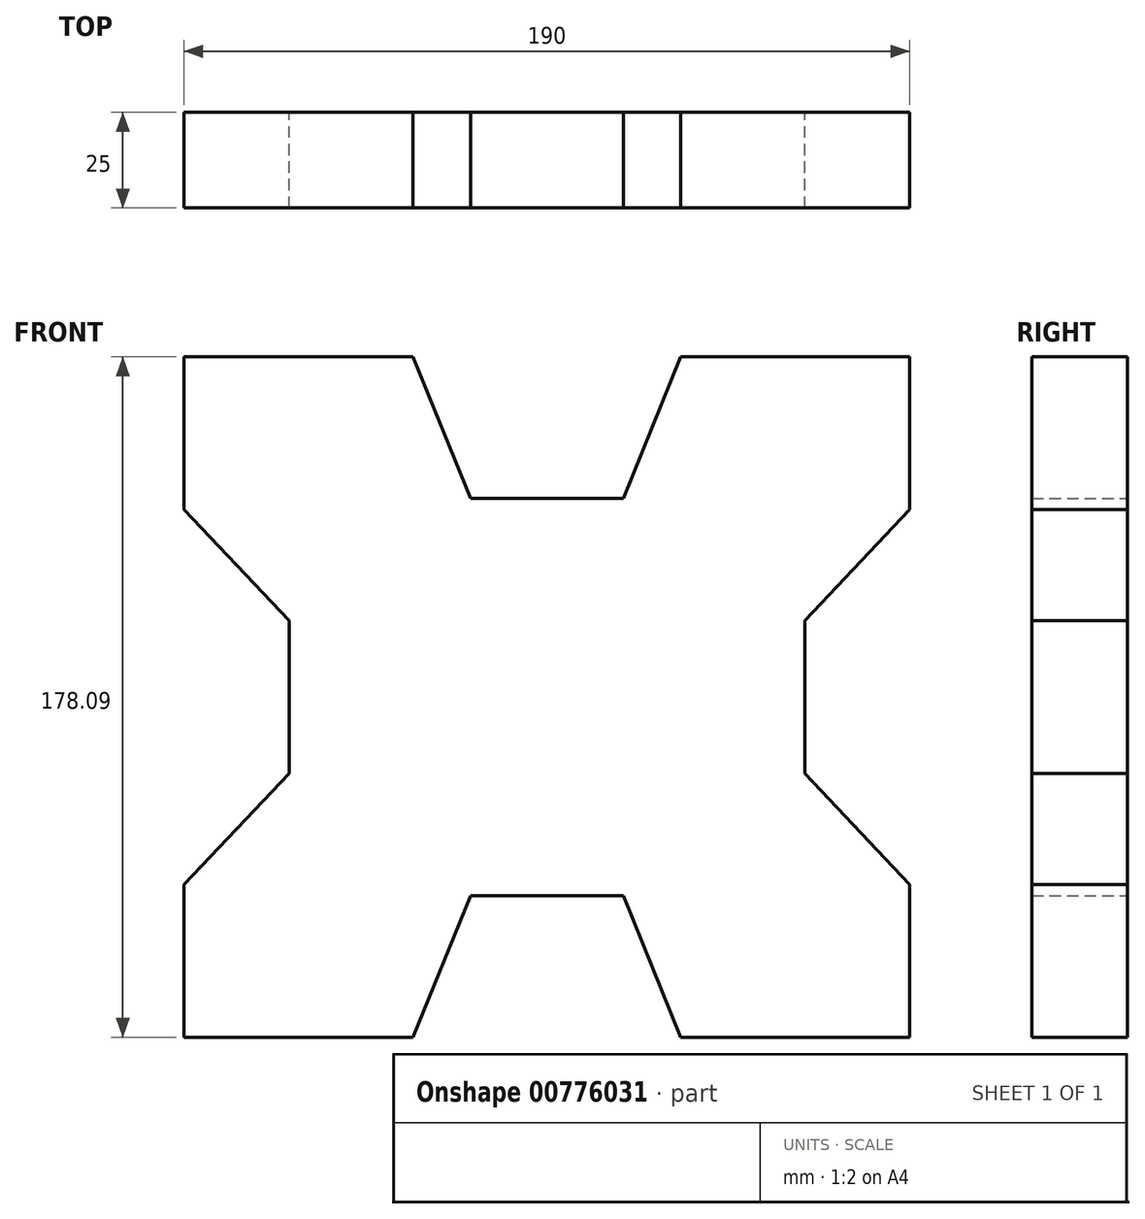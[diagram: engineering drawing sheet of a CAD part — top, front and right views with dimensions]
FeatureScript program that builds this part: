
annotation { "Feature Type Name" : "Feature", "Feature Type Description" : "" }
export const myFeature = defineFeature(function(context is Context, id is Id, definition is map)
    precondition{}
    {
        {
            var Q0;
            Q0=qCreatedBy(makeId("Front.planeOp"),FACE);
            var sketch = newSketch(context, id + "F0", { "sketchPlane" : qUnion([Q0])});
            skLineSegment(sketch, "E0", {"start": v(-65.6, 77.74) * mm, "end": v(-65.6, 37.74) * mm});
            skLineSegment(sketch, "E1", {"start": v(-65.6, -60.35) * mm, "end": v(-65.6, -100.35) * mm});
            skLineSegment(sketch, "E2", {"start": v(-65.6, -100.35) * mm, "end": v(-5.6, -100.35) * mm});
            skLineSegment(sketch, "E3", {"start": v(64.4, -100.35) * mm, "end": v(124.4, -100.35) * mm});
            skLineSegment(sketch, "E4", {"start": v(124.4, -100.35) * mm, "end": v(124.4, -60.35) * mm});
            skLineSegment(sketch, "E5", {"start": v(124.4, 37.74) * mm, "end": v(124.4, 77.74) * mm});
            skLineSegment(sketch, "E6", {"start": v(124.4, 77.74) * mm, "end": v(64.4, 77.74) * mm});
            skLineSegment(sketch, "E7", {"start": v(-5.6, 77.74) * mm, "end": v(-65.6, 77.74) * mm});
            skLineSegment(sketch, "E8", {"start": v(-38.1, 8.7) * mm, "end": v(-38.1, -31.3) * mm});
            skLineSegment(sketch, "E9", {"start": v(-65.6, 37.74) * mm, "end": v(-38.1, 8.7) * mm});
            skLineSegment(sketch, "E10", {"start": v(-65.6, -60.35) * mm, "end": v(-38.1, -31.3) * mm});
            skLineSegment(sketch, "E11", {"start": v(96.9, 8.7) * mm, "end": v(96.9, -31.3) * mm});
            skLineSegment(sketch, "E12", {"start": v(96.9, 8.7) * mm, "end": v(124.4, 37.74) * mm});
            skLineSegment(sketch, "E13", {"start": v(96.9, -31.3) * mm, "end": v(124.4, -60.35) * mm});
            skLineSegment(sketch, "E14", {"start": v(9.4, 40.66) * mm, "end": v(49.4, 40.66) * mm});
            skLineSegment(sketch, "E15", {"start": v(9.4, -63.27) * mm, "end": v(49.4, -63.27) * mm});
            skLineSegment(sketch, "E16", {"start": v(-5.6, -100.35) * mm, "end": v(9.4, -63.27) * mm});
            skLineSegment(sketch, "E17", {"start": v(64.4, -100.35) * mm, "end": v(49.4, -63.27) * mm});
            skLineSegment(sketch, "E18", {"start": v(49.4, 40.66) * mm, "end": v(64.4, 77.74) * mm});
            skLineSegment(sketch, "E19", {"start": v(9.4, 40.66) * mm, "end": v(-5.6, 77.74) * mm});
            skSolve(sketch);
        }
        {
            var Q0;
            Q0 = qSketchRegion(id + "F0", true);
            extrude(context, id + "F1", {"entities" : qUnion([Q0]), "depth" : 25 * mm, "offsetDistance" : 25 * mm});
        }
    });
